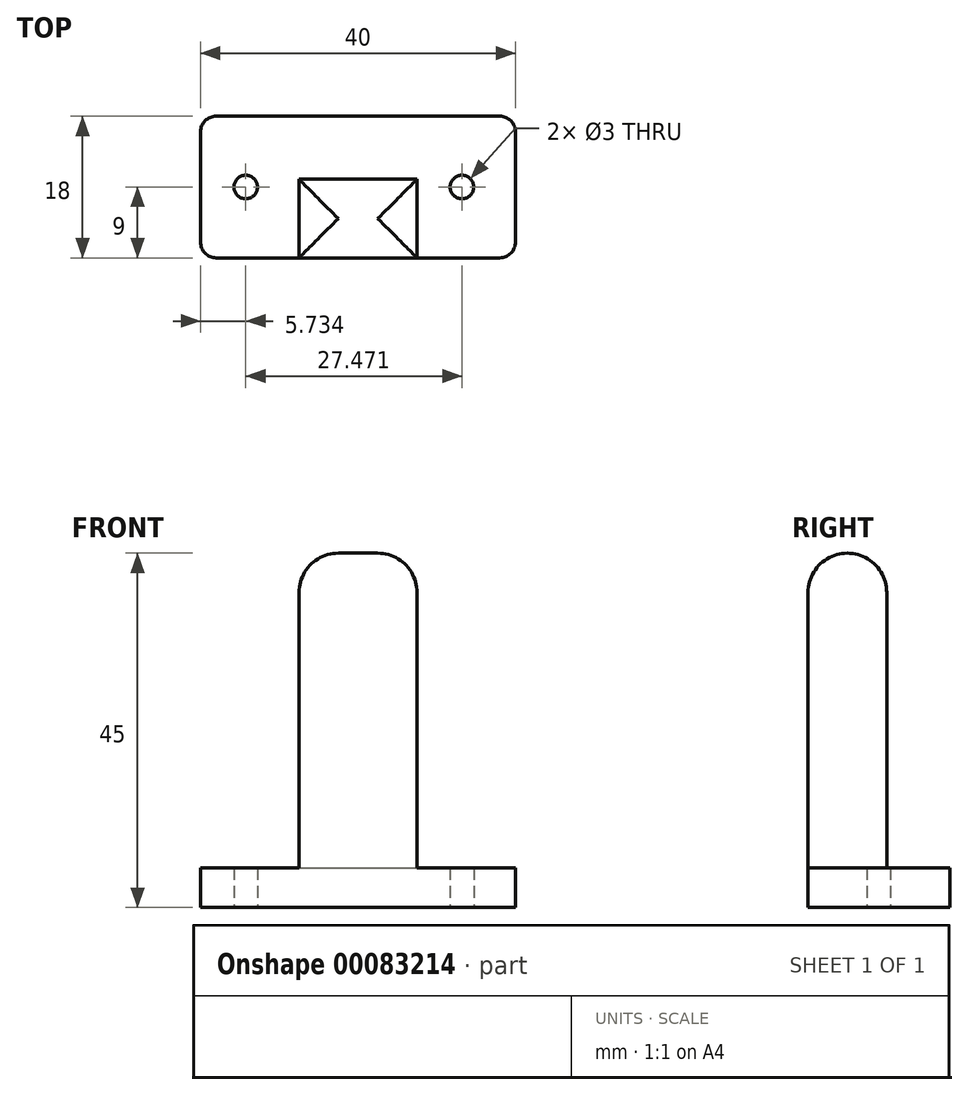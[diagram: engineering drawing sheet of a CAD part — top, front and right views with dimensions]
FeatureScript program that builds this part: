
annotation { "Feature Type Name" : "Feature", "Feature Type Description" : "" }
export const myFeature = defineFeature(function(context is Context, id is Id, definition is map)
    precondition{}
    {
        {
            var Q0;
            Q0=qCreatedBy(makeId("Top.planeOp"),FACE);
            var sketch = newSketch(context, id + "F0", { "sketchPlane" : qUnion([Q0])});
            skLineSegment(sketch, "E0.bottom", {"start": v(-20.08, 0) * mm, "end": v(19.92, 0) * mm});
            skLineSegment(sketch, "E0.top", {"start": v(-20.08, 18) * mm, "end": v(19.92, 18) * mm});
            skLineSegment(sketch, "E0.left", {"start": v(-20.08, 0) * mm, "end": v(-20.08, 18) * mm});
            skLineSegment(sketch, "E0.right", {"start": v(19.92, 0) * mm, "end": v(19.92, 18) * mm});
            skSolve(sketch);
        }
        {
            var Q0;
            Q0=makeQuery(id+"F0.imprint","IMPRINT",FACE,{"disambiguationData":[TD([[makeQuery(id+"F0.imprint","IMPRINT",EDGE,{"derivedFrom":sQuery(id+"F0.wireOp",EDGE,"E0.bottom")}),1.0]])]});
            extrude(context, id + "F1", {"entities" : qUnion([Q0]), "depth" : 5 * mm});
        }
        {
            var Q0;
            Q0=makeQuery(id+"F1.opExtrude","CAP_FACE",FACE,{"disambiguationData":[OSD([sQuery(id+"F0.wireOp",EDGE,"E0.bottom"),sQuery(id+"F0.wireOp",EDGE,"E0.top"),sQuery(id+"F0.wireOp",EDGE,"E0.left"),sQuery(id+"F0.wireOp",EDGE,"E0.right")])],"isStart":false});
            var sketch = newSketch(context, id + "F2", { "sketchPlane" : qUnion([Q0])});
            skLineSegment(sketch, "E1", {"start": v(-7.58, 0) * mm, "end": v(-7.58, 18) * mm});
            skLineSegment(sketch, "E2", {"start": v(7.42, 0) * mm, "end": v(7.42, 18) * mm});
            skLineSegment(sketch, "E3", {"start": v(-7.58, 10) * mm, "end": v(7.42, 10) * mm});
            skLineSegment(sketch, "E4", {"start": v(-14.35, 18) * mm, "end": v(-14.35, 0) * mm, "construction": true});
            skLineSegment(sketch, "E5", {"start": v(13.12, 18) * mm, "end": v(13.12, 0) * mm, "construction": true});
            skLineSegment(sketch, "E6", {"start": v(-20.08, 9) * mm, "end": v(19.92, 9) * mm, "construction": true});
            skPoint(sketch, "E7", {"position": v(-14.35, 9) * mm});
            skPoint(sketch, "E8", {"position": v(13.12, 9) * mm});
            skSolve(sketch);
        }
        {
            var Q0;
            {var subQ0=sQuery(id+"F2.wireOp",EDGE,"E3");Q0=makeQuery(id+"F2.imprint","IMPRINT",FACE,{"disambiguationData":[TD([[makeQuery(id+"F2.imprint","IMPRINT",EDGE,{"derivedFrom":subQ0}),-1.0]])]});}
            extrude(context, id + "F3", {"entities" : qUnion([Q0]), "operationType" : NewBodyOperationType.ADD, "depth" : 40 * mm});
        }
        {
            var Q0;
            Q0=makeQuery(id+"F3.opExtrude","CAP_EDGE",EDGE,{"disambiguationData":[OSD([sQuery(id+"F2.wireOp",EDGE,"E2")])],"isStart":false});
            var Q1;
            Q1=makeQuery(id+"F3.opExtrude","CAP_EDGE",EDGE,{"disambiguationData":[OSD([sQuery(id+"F2.wireOp",EDGE,"E3")])],"isStart":false});
            var Q2;
            Q2=makeQuery(id+"F3.opExtrude","CAP_EDGE",EDGE,{"disambiguationData":[OSD([sQuery(id+"F2.wireOp",EDGE,"E1")])],"isStart":false});
            var Q3;
            Q3=makeQuery(id+"F3.opExtrude","CAP_EDGE",EDGE,{"disambiguationData":[OSD([sQuery(id+"F0.wireOp",EDGE,"E0.bottom")])],"isStart":false});
            fillet(context, id + "F4", {"entities" : qUnion([Q0, Q1, Q2, Q3]), "radius" : 5 * mm, "tangentPropagation" : true, "allowEdgeOverflow" : false});
        }
        {
            var Q0;
            Q0=sQuery(id+"F2.wireOp",VERTEX,"E7");
            var Q1;
            Q1=sQuery(id+"F2.wireOp",VERTEX,"E8");
            var Q2;
            Q2=makeQuery(id+"F1.opExtrude","SWEPT_BODY",BODY,{"disambiguationData":[OSD([sQuery(id+"F0.wireOp",EDGE,"E0.bottom"),sQuery(id+"F0.wireOp",EDGE,"E0.top"),sQuery(id+"F0.wireOp",EDGE,"E0.left"),sQuery(id+"F0.wireOp",EDGE,"E0.right")])]});
            hole(context, id + "F5", {"style" : HoleStyle.SIMPLE, "endStyle" : HoleEndStyle.BLIND, "standardTappedOrClearance" : lookupTablePath({ "standard" : "ISO", "fit" : "Normal", "size" : "M5", "type" : "Clearance" }), "standardBlindInLast" : lookupTablePath({ "fit" : "Standard", "standard" : "ISO", "size" : "M5", "type" : "Clearance" }), "holeDiameter" : 3 * mm, "holeDepth" : 50 * mm, "locations" : qUnion([Q0, Q1]), "scope" : qUnion([Q2]), "startStyle" : HoleStartStyle.PART});
        }
        {
            var Q0;
            Q0=makeQuery(id+"F1.opExtrude","SWEPT_EDGE",EDGE,{"disambiguationData":[OSD([sQuery(id+"F0.wireOp",EDGE,"E0.bottom"),sQuery(id+"F0.wireOp",EDGE,"E0.left")])]});
            var Q1;
            Q1=makeQuery(id+"F1.opExtrude","SWEPT_EDGE",EDGE,{"disambiguationData":[OSD([sQuery(id+"F0.wireOp",EDGE,"E0.top"),sQuery(id+"F0.wireOp",EDGE,"E0.left")])]});
            var Q2;
            Q2=makeQuery(id+"F1.opExtrude","SWEPT_EDGE",EDGE,{"disambiguationData":[OSD([sQuery(id+"F0.wireOp",EDGE,"E0.top"),sQuery(id+"F0.wireOp",EDGE,"E0.right")])]});
            var Q3;
            Q3=makeQuery(id+"F1.opExtrude","SWEPT_EDGE",EDGE,{"disambiguationData":[OSD([sQuery(id+"F0.wireOp",EDGE,"E0.bottom"),sQuery(id+"F0.wireOp",EDGE,"E0.right")])]});
            fillet(context, id + "F6", {"entities" : qUnion([Q0, Q1, Q2, Q3]), "radius" : 2 * mm, "tangentPropagation" : true, "allowEdgeOverflow" : false});
        }
    });
